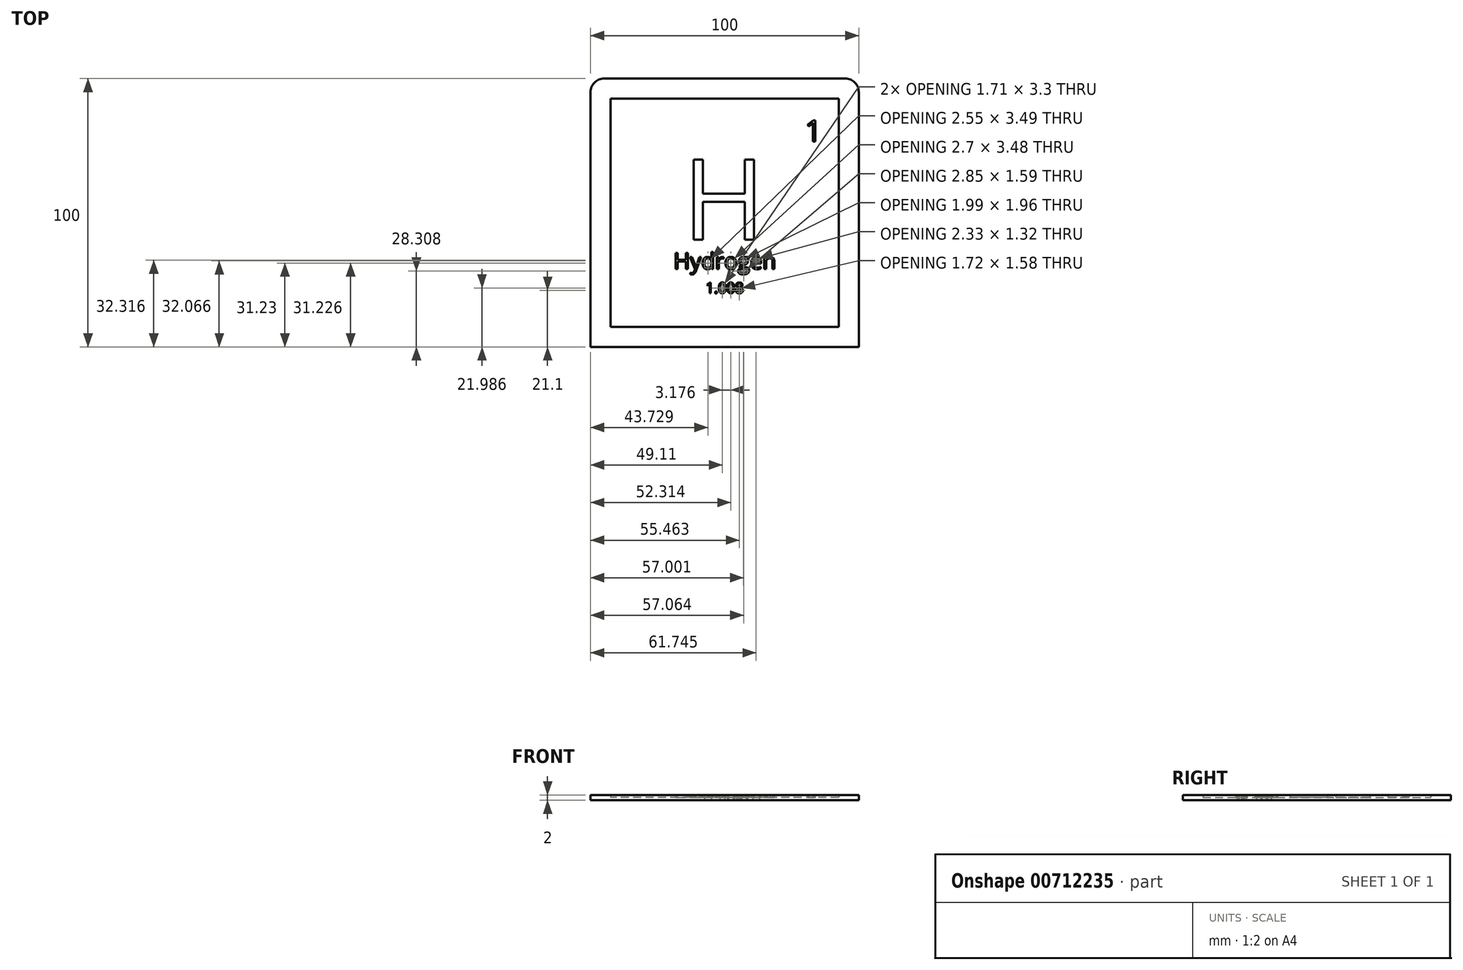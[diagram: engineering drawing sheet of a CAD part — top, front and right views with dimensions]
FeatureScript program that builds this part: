
annotation { "Feature Type Name" : "Feature", "Feature Type Description" : "" }
export const myFeature = defineFeature(function(context is Context, id is Id, definition is map)
    precondition{}
    {
        {
            var Q0;
            Q0=qCreatedBy(makeId("Top.planeOp"),FACE);
            var sketch = newSketch(context, id + "F0", { "sketchPlane" : qUnion([Q0])});
            skText(sketch, "E0", { "text": "H", "fontName": "OpenSans-Regular.ttf"});
            skLineSegment(sketch, "E1.bottom", {"start": v(42.5, -42.5) * mm, "end": v(-42.5, -42.5) * mm});
            skLineSegment(sketch, "E1.top", {"start": v(42.5, 42.5) * mm, "end": v(-42.5, 42.5) * mm});
            skLineSegment(sketch, "E1.left", {"start": v(42.5, -42.5) * mm, "end": v(42.5, 42.5) * mm});
            skLineSegment(sketch, "E1.right", {"start": v(-42.5, -42.5) * mm, "end": v(-42.5, 42.5) * mm});
            skPoint(sketch, "E1.middle", {"position": v(0, 0) * mm});
            skLineSegment(sketch, "E2.bottom", {"start": v(50, -50) * mm, "end": v(-50, -50) * mm});
            skLineSegment(sketch, "E2.top", {"start": v(50, 50) * mm, "end": v(-50, 50) * mm});
            skLineSegment(sketch, "E2.left", {"start": v(50, -50) * mm, "end": v(50, 50) * mm});
            skLineSegment(sketch, "E2.right", {"start": v(-50, -50) * mm, "end": v(-50, 50) * mm});
            skText(sketch, "E3", { "text": "1", "fontName": "OpenSans-Regular.ttf"});
            skText(sketch, "E4", { "text": "Hydrogen", "fontName": "OpenSans-Regular.ttf"});
            skText(sketch, "E5", { "text": "1.008", "fontName": "OpenSans-Regular.ttf"});
            const initialGuessF0  = {"E0": [-0.01569, -0.01, 1, 0, 0.03], "E3": [0.0299, 0.0265, 1, 0, 0.008], "E4": [-0.01906, -0.021, 1, 0, 0.006], "E5": [-0.00713, -0.03, 1, 0, 0.004]};
            skSetInitialGuess(sketch, initialGuessF0);
            skSolve(sketch);
        }
        {
            var Q0;
            Q0=makeQuery(id+"F0.imprint","IMPRINT",FACE,{"disambiguationData":[TD([[makeQuery(id+"F0.imprint","IMPRINT",EDGE,{"derivedFrom":sQuery(id+"F0.wireOp",EDGE,"E0.sketch_text.stroke-0")}),-1.0]])]});
            var Q1;
            Q1=makeQuery(id+"F0.imprint","IMPRINT",FACE,{"disambiguationData":[TD([[makeQuery(id+"F0.imprint","IMPRINT",EDGE,{"derivedFrom":sQuery(id+"F0.wireOp",EDGE,"E3.sketch_text.stroke-0")}),-1.0]])]});
            var Q2;
            Q2=makeQuery(id+"F0.imprint","IMPRINT",FACE,{"disambiguationData":[TD([[makeQuery(id+"F0.imprint","IMPRINT",EDGE,{"derivedFrom":sQuery(id+"F0.wireOp",EDGE,"E1.bottom")}),1.0]])]});
            var Q3;
            Q3=makeQuery(id+"F0.imprint","IMPRINT",FACE,{"disambiguationData":[TD([[makeQuery(id+"F0.imprint","IMPRINT",EDGE,{"derivedFrom":sQuery(id+"F0.wireOp",EDGE,"E4.sketch_text.stroke-0")}),-1.0]])]});
            var Q4;
            Q4=makeQuery(id+"F0.imprint","IMPRINT",FACE,{"disambiguationData":[TD([[makeQuery(id+"F0.imprint","IMPRINT",EDGE,{"derivedFrom":sQuery(id+"F0.wireOp",EDGE,"E4.sketch_text.stroke-12")}),-1.0]])]});
            var Q5;
            Q5=makeQuery(id+"F0.imprint","IMPRINT",FACE,{"disambiguationData":[TD([[makeQuery(id+"F0.imprint","IMPRINT",EDGE,{"derivedFrom":sQuery(id+"F0.wireOp",EDGE,"E4.sketch_text.stroke-28")}),-1.0]])]});
            var Q6;
            Q6=makeQuery(id+"F0.imprint","IMPRINT",FACE,{"disambiguationData":[TD([[makeQuery(id+"F0.imprint","IMPRINT",EDGE,{"derivedFrom":sQuery(id+"F0.wireOp",EDGE,"E4.sketch_text.stroke-52")}),-1.0]])]});
            var Q7;
            Q7=makeQuery(id+"F0.imprint","IMPRINT",FACE,{"disambiguationData":[TD([[makeQuery(id+"F0.imprint","IMPRINT",EDGE,{"derivedFrom":sQuery(id+"F0.wireOp",EDGE,"E4.sketch_text.stroke-65")}),-1.0]])]});
            var Q8;
            Q8=makeQuery(id+"F0.imprint","IMPRINT",FACE,{"disambiguationData":[TD([[makeQuery(id+"F0.imprint","IMPRINT",EDGE,{"derivedFrom":sQuery(id+"F0.wireOp",EDGE,"E4.sketch_text.stroke-82")}),-1.0]])]});
            var Q9;
            Q9=makeQuery(id+"F0.imprint","IMPRINT",FACE,{"disambiguationData":[TD([[makeQuery(id+"F0.imprint","IMPRINT",EDGE,{"derivedFrom":sQuery(id+"F0.wireOp",EDGE,"E4.sketch_text.stroke-126")}),-1.0]])]});
            var Q10;
            Q10=makeQuery(id+"F0.imprint","IMPRINT",FACE,{"disambiguationData":[TD([[makeQuery(id+"F0.imprint","IMPRINT",EDGE,{"derivedFrom":sQuery(id+"F0.wireOp",EDGE,"E4.sketch_text.stroke-145")}),-1.0]])]});
            var Q11;
            Q11=makeQuery(id+"F0.imprint","IMPRINT",FACE,{"disambiguationData":[TD([[makeQuery(id+"F0.imprint","IMPRINT",EDGE,{"derivedFrom":sQuery(id+"F0.wireOp",EDGE,"E5.sketch_text.stroke-49")}),-1.0]])]});
            var Q12;
            Q12=makeQuery(id+"F0.imprint","IMPRINT",FACE,{"disambiguationData":[TD([[makeQuery(id+"F0.imprint","IMPRINT",EDGE,{"derivedFrom":sQuery(id+"F0.wireOp",EDGE,"E5.sketch_text.stroke-33")}),-1.0]])]});
            var Q13;
            Q13=makeQuery(id+"F0.imprint","IMPRINT",FACE,{"disambiguationData":[TD([[makeQuery(id+"F0.imprint","IMPRINT",EDGE,{"derivedFrom":sQuery(id+"F0.wireOp",EDGE,"E5.sketch_text.stroke-17")}),-1.0]])]});
            var Q14;
            Q14=makeQuery(id+"F0.imprint","IMPRINT",FACE,{"disambiguationData":[TD([[makeQuery(id+"F0.imprint","IMPRINT",EDGE,{"derivedFrom":sQuery(id+"F0.wireOp",EDGE,"E5.sketch_text.stroke-9")}),-1.0]])]});
            var Q15;
            Q15=makeQuery(id+"F0.imprint","IMPRINT",FACE,{"disambiguationData":[TD([[makeQuery(id+"F0.imprint","IMPRINT",EDGE,{"derivedFrom":sQuery(id+"F0.wireOp",EDGE,"E5.sketch_text.stroke-0")}),-1.0]])]});
            extrude(context, id + "F1", {"entities" : qUnion([Q0, Q1, Q2, Q3, Q4, Q5, Q6, Q7, Q8, Q9, Q10, Q11, Q12, Q13, Q14, Q15]), "depth" : 2 * mm, "offsetDistance" : 25 * mm});
        }
        {
            var Q0;
            Q0=makeQuery(id+"F1.opExtrude","SWEPT_EDGE",EDGE,{"disambiguationData":[OSD([sQuery(id+"F0.wireOp",EDGE,"E2.top"),sQuery(id+"F0.wireOp",EDGE,"E2.left")])]});
            var Q1;
            Q1=makeQuery(id+"F1.opExtrude","SWEPT_EDGE",EDGE,{"disambiguationData":[OSD([sQuery(id+"F0.wireOp",EDGE,"E2.top"),sQuery(id+"F0.wireOp",EDGE,"E2.right")])]});
            fillet(context, id + "F2", {"entities" : qUnion([Q0, Q1]), "radius" : 5 * mm, "tangentPropagation" : true, "allowEdgeOverflow" : false});
        }
        {
            var Q0;
            Q0=qCreatedBy(makeId("Top.planeOp"),FACE);
            var sketch = newSketch(context, id + "F3", { "sketchPlane" : qUnion([Q0])});
            skText(sketch, "E6", { "text": "Li", "fontName": "OpenSans-Regular.ttf"});
            skLineSegment(sketch, "E7.bottom", {"start": v(42.5, -142.5) * mm, "end": v(-42.5, -142.5) * mm});
            skLineSegment(sketch, "E7.top", {"start": v(42.5, -57.5) * mm, "end": v(-42.5, -57.5) * mm});
            skLineSegment(sketch, "E7.left", {"start": v(42.5, -142.5) * mm, "end": v(42.5, -57.5) * mm});
            skLineSegment(sketch, "E7.right", {"start": v(-42.5, -142.5) * mm, "end": v(-42.5, -57.5) * mm});
            skPoint(sketch, "E7.middle", {"position": v(0, -100) * mm});
            skLineSegment(sketch, "E8.bottom", {"start": v(50, -150) * mm, "end": v(-50, -150) * mm});
            skLineSegment(sketch, "E8.top", {"start": v(50, -50) * mm, "end": v(-50, -50) * mm});
            skLineSegment(sketch, "E8.left", {"start": v(50, -150) * mm, "end": v(50, -50) * mm});
            skLineSegment(sketch, "E8.right", {"start": v(-50, -150) * mm, "end": v(-50, -50) * mm});
            skText(sketch, "E9", { "text": "3", "fontName": "OpenSans-Regular.ttf"});
            skText(sketch, "E10", { "text": "Lithium", "fontName": "OpenSans-Regular.ttf"});
            skText(sketch, "E11", { "text": "6.941", "fontName": "OpenSans-Regular.ttf"});
            const initialGuessF3  = {"E6": [-0.01548, -0.11, 1, 0, 0.03], "E9": [0.02808, -0.0735, 1, 0, 0.008], "E10": [-0.01466, -0.121, 1, 0, 0.006], "E11": [-0.00665, -0.13, 1, 0, 0.004]};
            skSetInitialGuess(sketch, initialGuessF3);
            skSolve(sketch);
        }
        {
            var Q0;
            Q0=makeQuery(id+"F0.imprint","IMPRINT",FACE,{"disambiguationData":[TD([[makeQuery(id+"F0.imprint","IMPRINT",EDGE,{"derivedFrom":sQuery(id+"F0.wireOp",EDGE,"E0.sketch_text.stroke-0")}),1.0]])]});
            extrude(context, id + "F4", {"entities" : qUnion([Q0]), "operationType" : NewBodyOperationType.ADD, "depth" : 1 * mm, "offsetDistance" : 25 * mm});
        }
    });
